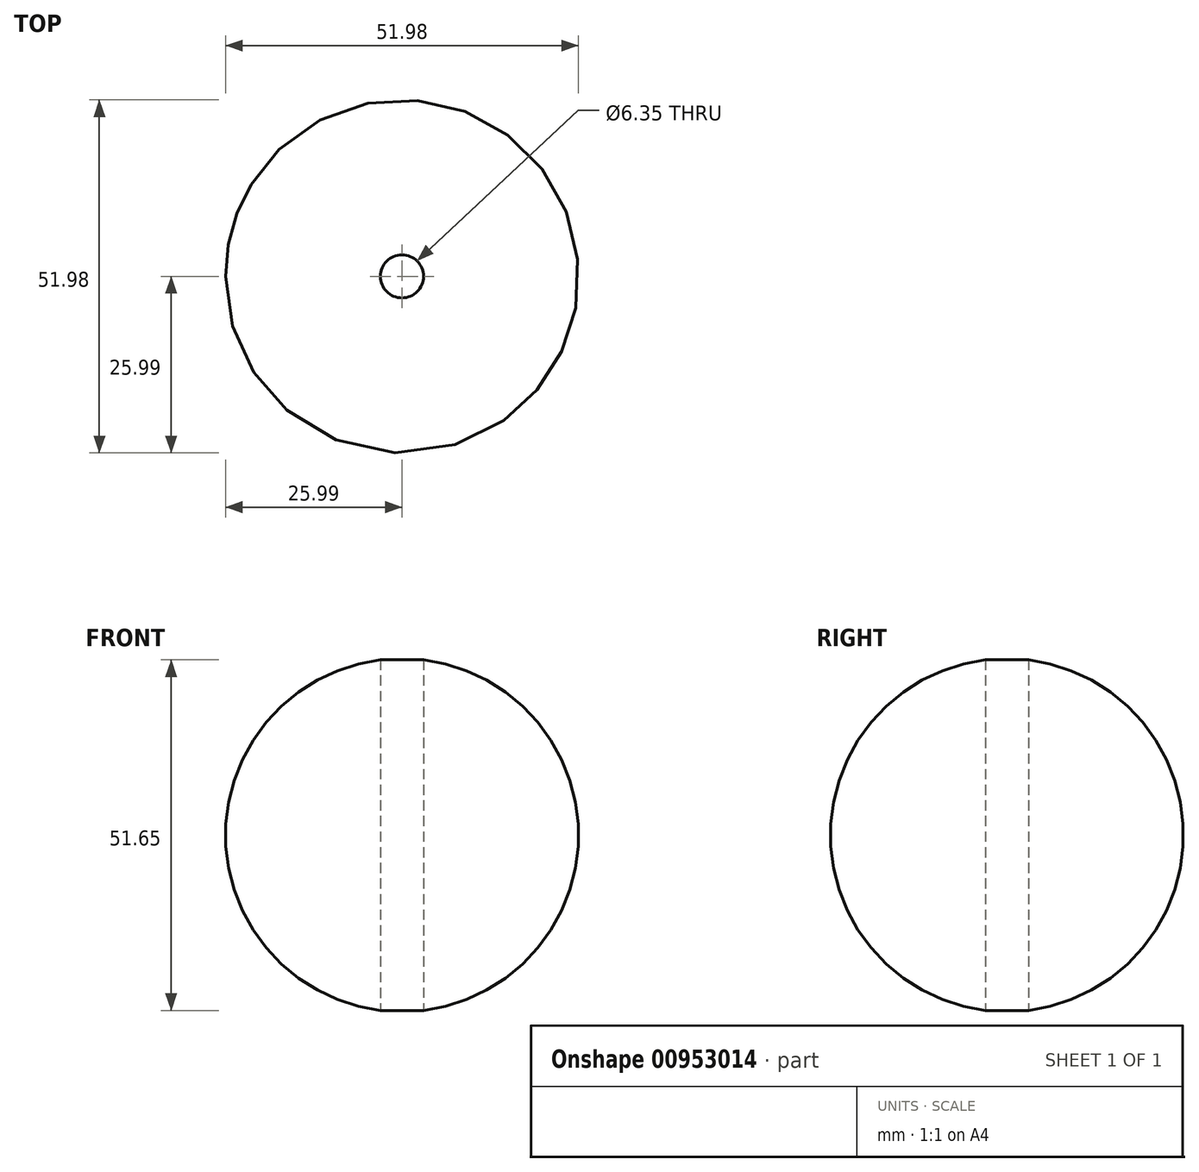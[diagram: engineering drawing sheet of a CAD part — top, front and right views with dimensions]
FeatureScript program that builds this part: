
annotation { "Feature Type Name" : "Feature", "Feature Type Description" : "" }
export const myFeature = defineFeature(function(context is Context, id is Id, definition is map)
    precondition{}
    {
        {
            var Q0;
            Q0=qCreatedBy(makeId("Front.planeOp"),FACE);
            var sketch = newSketch(context, id + "F0", { "sketchPlane" : qUnion([Q0])});
            skLineSegment(sketch, "E0", {"start": v(0, 0) * mm, "end": v(0, 52.05) * mm});
            skArc(sketch, "E1", {"start": v(0, 52.05) * mm, "mid": v(-26, 26.02) * mm, "end": v(0, 0) * mm});
            skLineSegment(sketch, "E2", {"start": v(0, 52.05) * mm, "end": v(0, -23.95) * mm, "construction": true});
            skSolve(sketch);
        }
        {
            var Q0;
            Q0 = qSketchRegion(id + "F0", true);
            var Q1;
            Q1=sQuery(id+"F0.wireOp",EDGE,"E2");
            revolve(context, id + "F1", {"surfaceOperationType" : NewSurfaceOperationType.NEW, "entities" : qUnion([Q0]), "axis" : qUnion([Q1]), "revolveType" : RevolveType.FULL});
        }
        {
            var Q0;
            Q0=qCreatedBy(makeId("Top.planeOp"),FACE);
            var sketch = newSketch(context, id + "F2", { "sketchPlane" : qUnion([Q0])});
            skCircle(sketch, "E3", {"center": v(0, 0) * mm, "radius": 4.36 * mm});
            skSolve(sketch);
        }
        {
            var Q0;
            Q0=sQuery(id+"F2.wireOp",VERTEX,"E3.center");
            var Q1;
            Q1=makeQuery(id+"F1.opRevolve","SWEPT_BODY",BODY,{"disambiguationData":[OSD([sQuery(id+"F0.wireOp",EDGE,"E0"),sQuery(id+"F0.wireOp",EDGE,"E1")])]});
            hole(context, id + "F3", {"style" : HoleStyle.SIMPLE, "endStyle" : HoleEndStyle.THROUGH, "oppositeDirection" : true, "holeDiameter" : 6.35 * mm, "majorDiameter" : 6.35 * mm, "isTappedThrough" : true, "tappedDepth" : 12.7 * mm, "tapClearance" : 3, "locations" : qUnion([Q0]), "scope" : qUnion([Q1])});
        }
    });
